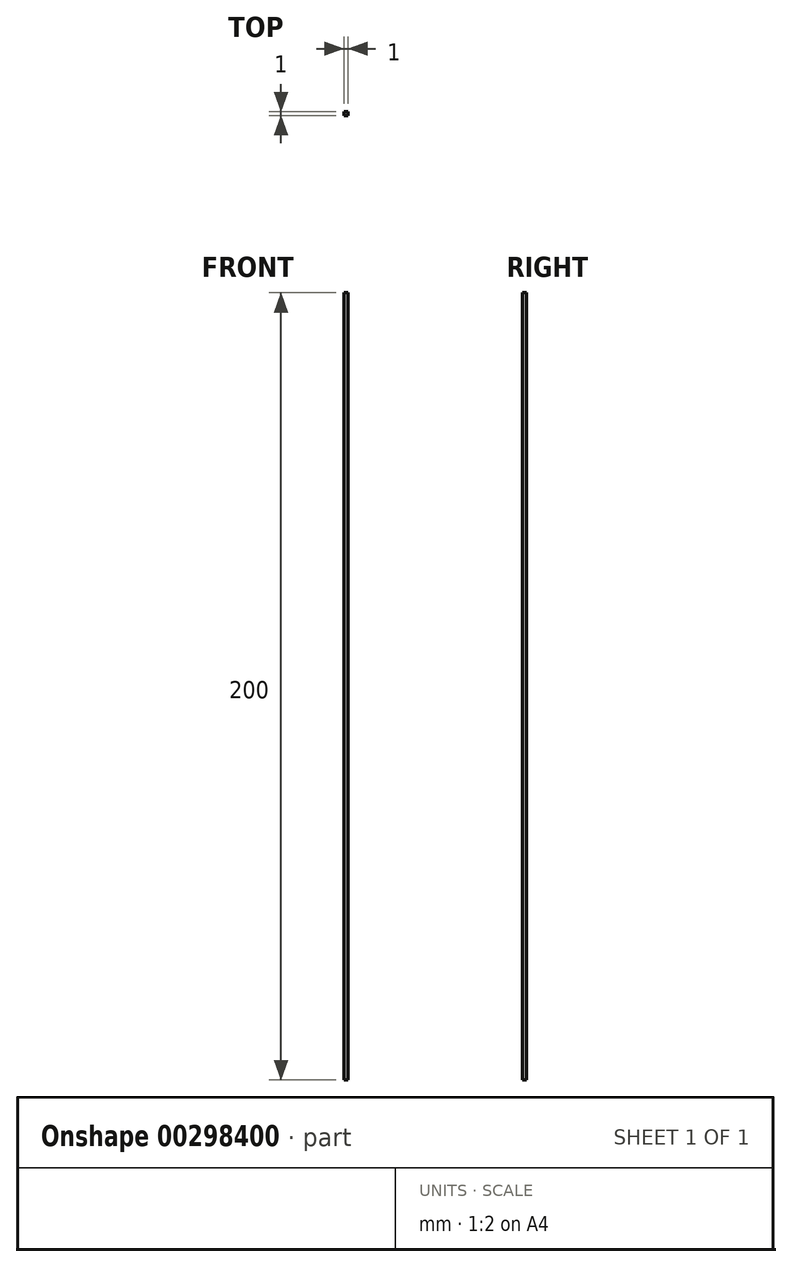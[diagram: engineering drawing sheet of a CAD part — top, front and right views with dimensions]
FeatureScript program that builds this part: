
annotation { "Feature Type Name" : "Feature", "Feature Type Description" : "" }
export const myFeature = defineFeature(function(context is Context, id is Id, definition is map)
    precondition{}
    {
        {
            var Q0;
            Q0=qCreatedBy(makeId("Top.planeOp"),FACE);
            var sketch = newSketch(context, id + "F0", { "sketchPlane" : qUnion([Q0])});
            skLineSegment(sketch, "E0.bottom", {"start": v(0.5, 0.5) * mm, "end": v(-0.5, 0.5) * mm});
            skLineSegment(sketch, "E0.top", {"start": v(0.5, -0.5) * mm, "end": v(-0.5, -0.5) * mm});
            skLineSegment(sketch, "E0.left", {"start": v(0.5, 0.5) * mm, "end": v(0.5, -0.5) * mm});
            skLineSegment(sketch, "E0.right", {"start": v(-0.5, 0.5) * mm, "end": v(-0.5, -0.5) * mm});
            skPoint(sketch, "E0.middle", {"position": v(0, 0) * mm});
            skSolve(sketch);
        }
        {
            var Q0;
            Q0 = qSketchRegion(id + "F0", true);
            extrude(context, id + "F1", {"entities" : qUnion([Q0]), "depth" : 200 * mm});
        }
    });
